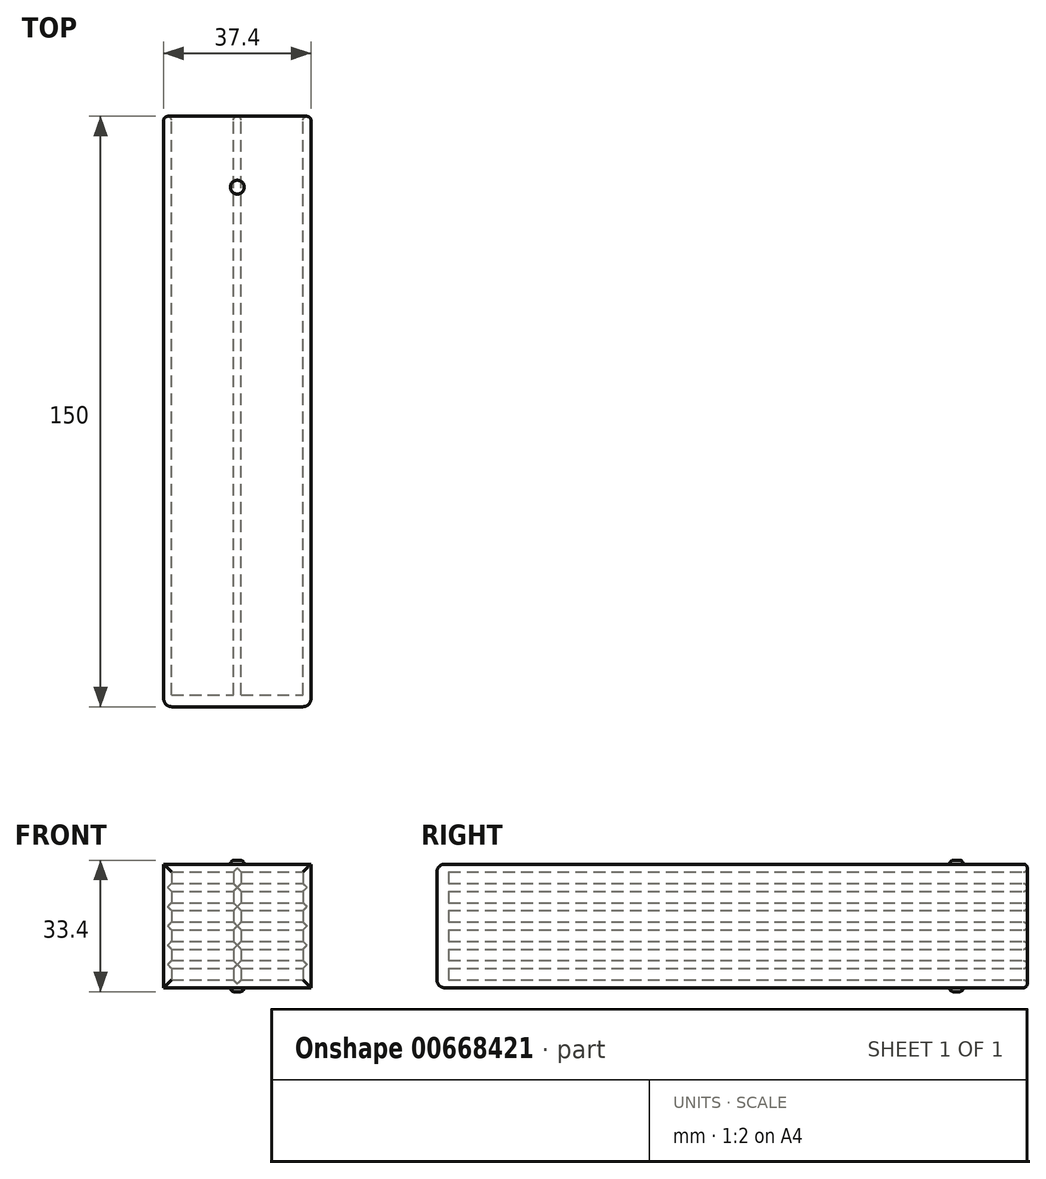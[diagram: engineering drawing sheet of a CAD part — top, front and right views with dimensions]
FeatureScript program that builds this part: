
annotation { "Feature Type Name" : "Feature", "Feature Type Description" : "" }
export const myFeature = defineFeature(function(context is Context, id is Id, definition is map)
    precondition{}
    {
        {
            var Q0;
            Q0=qCreatedBy(makeId("Front.planeOp"),FACE);
            var sketch = newSketch(context, id + "F0", { "sketchPlane" : qUnion([Q0])});
            skLineSegment(sketch, "E0.bottom", {"start": v(-15.7, -3.54) * mm, "end": v(0, -3.54) * mm});
            skLineSegment(sketch, "E0.top", {"start": v(-15.7, -6.44) * mm, "end": v(0, -6.44) * mm});
            skLineSegment(sketch, "E0.left", {"start": v(-15.7, -3.54) * mm, "end": v(-15.7, -6.44) * mm});
            skLineSegment(sketch, "E0.right", {"start": v(0, -3.54) * mm, "end": v(0, -6.44) * mm});
            skLineSegment(sketch, "E1.0.1.0", {"start": v(2, -3.54) * mm, "end": v(17.7, -3.54) * mm});
            skLineSegment(sketch, "E1.0.1.1", {"start": v(2, -6.44) * mm, "end": v(17.7, -6.44) * mm});
            skLineSegment(sketch, "E1.0.1.2", {"start": v(2, -3.54) * mm, "end": v(2, -6.44) * mm});
            skLineSegment(sketch, "E1.0.1.3", {"start": v(17.7, -3.54) * mm, "end": v(17.7, -6.44) * mm});
            skLineSegment(sketch, "E1.1.0.0", {"start": v(-15.7, -8.44) * mm, "end": v(0, -8.44) * mm});
            skLineSegment(sketch, "E1.1.0.1", {"start": v(-15.7, -11.34) * mm, "end": v(0, -11.34) * mm});
            skLineSegment(sketch, "E1.1.0.2", {"start": v(-15.7, -8.44) * mm, "end": v(-15.7, -11.34) * mm});
            skLineSegment(sketch, "E1.1.0.3", {"start": v(0, -8.44) * mm, "end": v(0, -11.34) * mm});
            skLineSegment(sketch, "E1.1.1.0", {"start": v(2, -8.44) * mm, "end": v(17.7, -8.44) * mm});
            skLineSegment(sketch, "E1.1.1.1", {"start": v(2, -11.34) * mm, "end": v(17.7, -11.34) * mm});
            skLineSegment(sketch, "E1.1.1.2", {"start": v(2, -8.44) * mm, "end": v(2, -11.34) * mm});
            skLineSegment(sketch, "E1.1.1.3", {"start": v(17.7, -8.44) * mm, "end": v(17.7, -11.34) * mm});
            skLineSegment(sketch, "E1.2.0.0", {"start": v(-15.7, -13.34) * mm, "end": v(0, -13.34) * mm});
            skLineSegment(sketch, "E1.2.0.1", {"start": v(-15.7, -16.24) * mm, "end": v(0, -16.24) * mm});
            skLineSegment(sketch, "E1.2.0.2", {"start": v(-15.7, -13.34) * mm, "end": v(-15.7, -16.24) * mm});
            skLineSegment(sketch, "E1.2.0.3", {"start": v(0, -13.34) * mm, "end": v(0, -16.24) * mm});
            skLineSegment(sketch, "E1.2.1.0", {"start": v(2, -13.34) * mm, "end": v(17.7, -13.34) * mm});
            skLineSegment(sketch, "E1.2.1.1", {"start": v(2, -16.24) * mm, "end": v(17.7, -16.24) * mm});
            skLineSegment(sketch, "E1.2.1.2", {"start": v(2, -13.34) * mm, "end": v(2, -16.24) * mm});
            skLineSegment(sketch, "E1.2.1.3", {"start": v(17.7, -13.34) * mm, "end": v(17.7, -16.24) * mm});
            skLineSegment(sketch, "E1.3.0.0", {"start": v(-15.7, -18.24) * mm, "end": v(0, -18.24) * mm});
            skLineSegment(sketch, "E1.3.0.1", {"start": v(-15.7, -21.14) * mm, "end": v(0, -21.14) * mm});
            skLineSegment(sketch, "E1.3.0.2", {"start": v(-15.7, -18.24) * mm, "end": v(-15.7, -21.14) * mm});
            skLineSegment(sketch, "E1.3.0.3", {"start": v(0, -18.24) * mm, "end": v(0, -21.14) * mm});
            skLineSegment(sketch, "E1.3.1.0", {"start": v(2, -18.24) * mm, "end": v(17.7, -18.24) * mm});
            skLineSegment(sketch, "E1.3.1.1", {"start": v(2, -21.14) * mm, "end": v(17.7, -21.14) * mm});
            skLineSegment(sketch, "E1.3.1.2", {"start": v(2, -18.24) * mm, "end": v(2, -21.14) * mm});
            skLineSegment(sketch, "E1.3.1.3", {"start": v(17.7, -18.24) * mm, "end": v(17.7, -21.14) * mm});
            skLineSegment(sketch, "E1.4.0.0", {"start": v(-15.7, -23.14) * mm, "end": v(0, -23.14) * mm});
            skLineSegment(sketch, "E1.4.0.1", {"start": v(-15.7, -26.04) * mm, "end": v(0, -26.04) * mm});
            skLineSegment(sketch, "E1.4.0.2", {"start": v(-15.7, -23.14) * mm, "end": v(-15.7, -26.04) * mm});
            skLineSegment(sketch, "E1.4.0.3", {"start": v(0, -23.14) * mm, "end": v(0, -26.04) * mm});
            skLineSegment(sketch, "E1.4.1.0", {"start": v(2, -23.14) * mm, "end": v(17.7, -23.14) * mm});
            skLineSegment(sketch, "E1.4.1.1", {"start": v(2, -26.04) * mm, "end": v(17.7, -26.04) * mm});
            skLineSegment(sketch, "E1.4.1.2", {"start": v(2, -23.14) * mm, "end": v(2, -26.04) * mm});
            skLineSegment(sketch, "E1.4.1.3", {"start": v(17.7, -23.14) * mm, "end": v(17.7, -26.04) * mm});
            skLineSegment(sketch, "E1.5.0.0", {"start": v(-15.7, -28.04) * mm, "end": v(0, -28.04) * mm});
            skLineSegment(sketch, "E1.5.0.1", {"start": v(-15.7, -30.94) * mm, "end": v(0, -30.94) * mm});
            skLineSegment(sketch, "E1.5.0.2", {"start": v(-15.7, -28.04) * mm, "end": v(-15.7, -30.94) * mm});
            skLineSegment(sketch, "E1.5.0.3", {"start": v(0, -28.04) * mm, "end": v(0, -30.94) * mm});
            skLineSegment(sketch, "E1.5.1.0", {"start": v(2, -28.04) * mm, "end": v(17.7, -28.04) * mm});
            skLineSegment(sketch, "E1.5.1.1", {"start": v(2, -30.94) * mm, "end": v(17.7, -30.94) * mm});
            skLineSegment(sketch, "E1.5.1.2", {"start": v(2, -28.04) * mm, "end": v(2, -30.94) * mm});
            skLineSegment(sketch, "E1.5.1.3", {"start": v(17.7, -28.04) * mm, "end": v(17.7, -30.94) * mm});
            skLineSegment(sketch, "E1.direction1", {"start": v(-15.7, -3.54) * mm, "end": v(-15.7, -8.44) * mm, "construction": true});
            skLineSegment(sketch, "E1.direction2", {"start": v(-15.7, -3.54) * mm, "end": v(2, -3.54) * mm, "construction": true});
            skLineSegment(sketch, "E2.bottom", {"start": v(-17.7, -1.54) * mm, "end": v(19.7, -1.54) * mm});
            skLineSegment(sketch, "E2.top", {"start": v(-17.7, -32.94) * mm, "end": v(19.7, -32.94) * mm});
            skLineSegment(sketch, "E2.left", {"start": v(-17.7, -1.54) * mm, "end": v(-17.7, -32.94) * mm});
            skLineSegment(sketch, "E2.right", {"start": v(19.7, -1.54) * mm, "end": v(19.7, -32.94) * mm});
            skSolve(sketch);
        }
        {
            var Q0;
            Q0 = qSketchRegion(id + "F0", true);
            extrude(context, id + "F1", {"entities" : qUnion([Q0]), "depth" : 147 * mm, "offsetDistance" : 25 * mm});
        }
        {
            var Q0;
            Q0=makeQuery(id+"F1.opExtrude","CAP_FACE",FACE,{"disambiguationData":[OSD([sQuery(id+"F0.wireOp",EDGE,"E0.bottom"),sQuery(id+"F0.wireOp",EDGE,"E0.top"),sQuery(id+"F0.wireOp",EDGE,"E0.left"),sQuery(id+"F0.wireOp",EDGE,"E0.right"),sQuery(id+"F0.wireOp",EDGE,"E1.0.1.0"),sQuery(id+"F0.wireOp",EDGE,"E1.0.1.1"),sQuery(id+"F0.wireOp",EDGE,"E1.0.1.2"),sQuery(id+"F0.wireOp",EDGE,"E1.0.1.3"),sQuery(id+"F0.wireOp",EDGE,"E1.1.0.0"),sQuery(id+"F0.wireOp",EDGE,"E1.1.0.1"),sQuery(id+"F0.wireOp",EDGE,"E1.1.0.2"),sQuery(id+"F0.wireOp",EDGE,"E1.1.0.3"),sQuery(id+"F0.wireOp",EDGE,"E1.1.1.0"),sQuery(id+"F0.wireOp",EDGE,"E1.1.1.1"),sQuery(id+"F0.wireOp",EDGE,"E1.1.1.2"),sQuery(id+"F0.wireOp",EDGE,"E1.1.1.3"),sQuery(id+"F0.wireOp",EDGE,"E1.2.0.0"),sQuery(id+"F0.wireOp",EDGE,"E1.2.0.1"),sQuery(id+"F0.wireOp",EDGE,"E1.2.0.2"),sQuery(id+"F0.wireOp",EDGE,"E1.2.0.3"),sQuery(id+"F0.wireOp",EDGE,"E1.2.1.0"),sQuery(id+"F0.wireOp",EDGE,"E1.2.1.1"),sQuery(id+"F0.wireOp",EDGE,"E1.2.1.2"),sQuery(id+"F0.wireOp",EDGE,"E1.2.1.3"),sQuery(id+"F0.wireOp",EDGE,"E1.3.0.0"),sQuery(id+"F0.wireOp",EDGE,"E1.3.0.1"),sQuery(id+"F0.wireOp",EDGE,"E1.3.0.2"),sQuery(id+"F0.wireOp",EDGE,"E1.3.0.3"),sQuery(id+"F0.wireOp",EDGE,"E1.3.1.0"),sQuery(id+"F0.wireOp",EDGE,"E1.3.1.1"),sQuery(id+"F0.wireOp",EDGE,"E1.3.1.2"),sQuery(id+"F0.wireOp",EDGE,"E1.3.1.3"),sQuery(id+"F0.wireOp",EDGE,"E1.4.0.0"),sQuery(id+"F0.wireOp",EDGE,"E1.4.0.1"),sQuery(id+"F0.wireOp",EDGE,"E1.4.0.2"),sQuery(id+"F0.wireOp",EDGE,"E1.4.0.3"),sQuery(id+"F0.wireOp",EDGE,"E1.4.1.0"),sQuery(id+"F0.wireOp",EDGE,"E1.4.1.1"),sQuery(id+"F0.wireOp",EDGE,"E1.4.1.2"),sQuery(id+"F0.wireOp",EDGE,"E1.4.1.3"),sQuery(id+"F0.wireOp",EDGE,"E1.5.0.0"),sQuery(id+"F0.wireOp",EDGE,"E1.5.0.1"),sQuery(id+"F0.wireOp",EDGE,"E1.5.0.2"),sQuery(id+"F0.wireOp",EDGE,"E1.5.0.3"),sQuery(id+"F0.wireOp",EDGE,"E1.5.1.0"),sQuery(id+"F0.wireOp",EDGE,"E1.5.1.1"),sQuery(id+"F0.wireOp",EDGE,"E1.5.1.2"),sQuery(id+"F0.wireOp",EDGE,"E1.5.1.3"),sQuery(id+"F0.wireOp",EDGE,"E2.bottom"),sQuery(id+"F0.wireOp",EDGE,"E2.top"),sQuery(id+"F0.wireOp",EDGE,"E2.left"),sQuery(id+"F0.wireOp",EDGE,"E2.right")])],"isStart":false});
            var sketch = newSketch(context, id + "F2", { "sketchPlane" : qUnion([Q0])});
            skLineSegment(sketch, "E3.bottom", {"start": v(-17.7, -1.54) * mm, "end": v(19.7, -1.54) * mm});
            skLineSegment(sketch, "E3.top", {"start": v(-17.7, -32.94) * mm, "end": v(19.7, -32.94) * mm});
            skLineSegment(sketch, "E3.left", {"start": v(-17.7, -1.54) * mm, "end": v(-17.7, -32.94) * mm});
            skLineSegment(sketch, "E3.right", {"start": v(19.7, -1.54) * mm, "end": v(19.7, -32.94) * mm});
            skSolve(sketch);
        }
        {
            var Q0;
            Q0 = qSketchRegion(id + "F2", true);
            extrude(context, id + "F3", {"entities" : qUnion([Q0]), "operationType" : NewBodyOperationType.ADD, "depth" : 3 * mm, "offsetDistance" : 25 * mm});
        }
        {
            var Q0;
            Q0=makeQuery(id+"F3.opExtrude","CAP_FACE",FACE,{"disambiguationData":[OSD([sQuery(id+"F2.wireOp",EDGE,"E3.bottom"),sQuery(id+"F2.wireOp",EDGE,"E3.top"),sQuery(id+"F2.wireOp",EDGE,"E3.left"),sQuery(id+"F2.wireOp",EDGE,"E3.right")])],"isStart":false});
            fillet(context, id + "F4", {"entities" : qUnion([Q0]), "radius" : 2 * mm, "tangentPropagation" : true, "allowEdgeOverflow" : false});
        }
        {
            var Q0;
            Q0=makeQuery(id+"F1.opExtrude","CAP_FACE",FACE,{"disambiguationData":[OSD([sQuery(id+"F0.wireOp",EDGE,"E0.bottom"),sQuery(id+"F0.wireOp",EDGE,"E0.top"),sQuery(id+"F0.wireOp",EDGE,"E0.left"),sQuery(id+"F0.wireOp",EDGE,"E0.right"),sQuery(id+"F0.wireOp",EDGE,"E1.0.1.0"),sQuery(id+"F0.wireOp",EDGE,"E1.0.1.1"),sQuery(id+"F0.wireOp",EDGE,"E1.0.1.2"),sQuery(id+"F0.wireOp",EDGE,"E1.0.1.3"),sQuery(id+"F0.wireOp",EDGE,"E1.1.0.0"),sQuery(id+"F0.wireOp",EDGE,"E1.1.0.1"),sQuery(id+"F0.wireOp",EDGE,"E1.1.0.2"),sQuery(id+"F0.wireOp",EDGE,"E1.1.0.3"),sQuery(id+"F0.wireOp",EDGE,"E1.1.1.0"),sQuery(id+"F0.wireOp",EDGE,"E1.1.1.1"),sQuery(id+"F0.wireOp",EDGE,"E1.1.1.2"),sQuery(id+"F0.wireOp",EDGE,"E1.1.1.3"),sQuery(id+"F0.wireOp",EDGE,"E1.2.0.0"),sQuery(id+"F0.wireOp",EDGE,"E1.2.0.1"),sQuery(id+"F0.wireOp",EDGE,"E1.2.0.2"),sQuery(id+"F0.wireOp",EDGE,"E1.2.0.3"),sQuery(id+"F0.wireOp",EDGE,"E1.2.1.0"),sQuery(id+"F0.wireOp",EDGE,"E1.2.1.1"),sQuery(id+"F0.wireOp",EDGE,"E1.2.1.2"),sQuery(id+"F0.wireOp",EDGE,"E1.2.1.3"),sQuery(id+"F0.wireOp",EDGE,"E1.3.0.0"),sQuery(id+"F0.wireOp",EDGE,"E1.3.0.1"),sQuery(id+"F0.wireOp",EDGE,"E1.3.0.2"),sQuery(id+"F0.wireOp",EDGE,"E1.3.0.3"),sQuery(id+"F0.wireOp",EDGE,"E1.3.1.0"),sQuery(id+"F0.wireOp",EDGE,"E1.3.1.1"),sQuery(id+"F0.wireOp",EDGE,"E1.3.1.2"),sQuery(id+"F0.wireOp",EDGE,"E1.3.1.3"),sQuery(id+"F0.wireOp",EDGE,"E1.4.0.0"),sQuery(id+"F0.wireOp",EDGE,"E1.4.0.1"),sQuery(id+"F0.wireOp",EDGE,"E1.4.0.2"),sQuery(id+"F0.wireOp",EDGE,"E1.4.0.3"),sQuery(id+"F0.wireOp",EDGE,"E1.4.1.0"),sQuery(id+"F0.wireOp",EDGE,"E1.4.1.1"),sQuery(id+"F0.wireOp",EDGE,"E1.4.1.2"),sQuery(id+"F0.wireOp",EDGE,"E1.4.1.3"),sQuery(id+"F0.wireOp",EDGE,"E1.5.0.0"),sQuery(id+"F0.wireOp",EDGE,"E1.5.0.1"),sQuery(id+"F0.wireOp",EDGE,"E1.5.0.2"),sQuery(id+"F0.wireOp",EDGE,"E1.5.0.3"),sQuery(id+"F0.wireOp",EDGE,"E1.5.1.0"),sQuery(id+"F0.wireOp",EDGE,"E1.5.1.1"),sQuery(id+"F0.wireOp",EDGE,"E1.5.1.2"),sQuery(id+"F0.wireOp",EDGE,"E1.5.1.3"),sQuery(id+"F0.wireOp",EDGE,"E2.bottom"),sQuery(id+"F0.wireOp",EDGE,"E2.top"),sQuery(id+"F0.wireOp",EDGE,"E2.left"),sQuery(id+"F0.wireOp",EDGE,"E2.right")])],"isStart":true});
            fillet(context, id + "F5", {"entities" : qUnion([Q0]), "radius" : 1 * mm, "tangentPropagation" : true, "allowEdgeOverflow" : false});
        }
        {
            var Q0;
            Q0=makeQuery(id+"F3.boolean.opBoolean","MERGE",FACE,{"derivedFrom":[makeQuery(id+"F1.opExtrude","SWEPT_FACE",FACE,{"disambiguationData":[OSD([sQuery(id+"F0.wireOp",EDGE,"E2.top")])]}),makeQuery(id+"F3.opExtrude","SWEPT_FACE",FACE,{"disambiguationData":[OSD([sQuery(id+"F2.wireOp",EDGE,"E3.top")])]})]});
            var sketch = newSketch(context, id + "F6", { "sketchPlane" : qUnion([Q0])});
            skText(sketch, "E4", { "text": "flat file", "fontName": "OpenSans-Bold.ttf"});
            const initialGuessF6  = {"E4": [-0.008, 0.14531, 0, -1, 0.015]};
            skSetInitialGuess(sketch, initialGuessF6);
            skSolve(sketch);
        }
        {
            var Q0;
            Q0=makeQuery(id+"F3.boolean.opBoolean","MERGE",FACE,{"derivedFrom":[makeQuery(id+"F1.opExtrude","SWEPT_FACE",FACE,{"disambiguationData":[OSD([sQuery(id+"F0.wireOp",EDGE,"E2.bottom")])]}),makeQuery(id+"F3.opExtrude","SWEPT_FACE",FACE,{"disambiguationData":[OSD([sQuery(id+"F2.wireOp",EDGE,"E3.bottom")])]})]});
            var sketch = newSketch(context, id + "F7", { "sketchPlane" : qUnion([Q0])});
            skLineSegment(sketch, "E5", {"start": v(-16.7, 0) * mm, "end": v(18.7, 0) * mm});
            skLineSegment(sketch, "E6", {"start": v(-30.07, -18) * mm, "end": v(37.03, -18) * mm, "construction": true});
            skCircle(sketch, "E7", {"center": v(1, -18) * mm, "radius": 1.75 * mm});
            skLineSegment(sketch, "E8", {"start": v(1, -1) * mm, "end": v(1, -24.07) * mm, "construction": true});
            skSolve(sketch);
        }
        {
            var Q0;
            Q0 = qSketchRegion(id + "F7", true);
            extrude(context, id + "F8", {"entities" : qUnion([Q0]), "operationType" : NewBodyOperationType.ADD, "depth" : 1 * mm, "offsetDistance" : 25 * mm});
        }
        {
            var Q0;
            Q0=makeQuery(id+"F8.opExtrude","CAP_EDGE",EDGE,{"disambiguationData":[OSD([sQuery(id+"F7.wireOp",EDGE,"E7")])],"isStart":false});
            fillet(context, id + "F9", {"entities" : qUnion([Q0]), "radius" : 1 * mm, "tangentPropagation" : true, "allowEdgeOverflow" : false});
        }
        {
            var Q0;
            Q0=makeQuery(id+"F3.boolean.opBoolean","MERGE",FACE,{"derivedFrom":[makeQuery(id+"F1.opExtrude","SWEPT_FACE",FACE,{"disambiguationData":[OSD([sQuery(id+"F0.wireOp",EDGE,"E2.bottom")])]}),makeQuery(id+"F3.opExtrude","SWEPT_FACE",FACE,{"disambiguationData":[OSD([sQuery(id+"F2.wireOp",EDGE,"E3.bottom")])]})]});
            var sketch = newSketch(context, id + "F10", { "sketchPlane" : qUnion([Q0])});
            skCircle(sketch, "E9.0", {"center": v(1, -18) * mm, "radius": 1.75 * mm});
            skCircle(sketch, "E9.1", {"center": v(1, -18) * mm, "radius": 0.75 * mm});
            skSolve(sketch);
        }
        {
            var Q0;
            Q0=makeQuery(id+"F6.imprint","IMPRINT",FACE,{"disambiguationData":[TD([[makeQuery(id+"F6.imprint","IMPRINT",EDGE,{"derivedFrom":sQuery(id+"F6.wireOp",EDGE,"E4.sketch_text.stroke-0")}),1.0]])]});
            var sketch = newSketch(context, id + "F11", { "sketchPlane" : qUnion([Q0])});
            skCircle(sketch, "E10.0", {"center": v(1, 18) * mm, "radius": 1.75 * mm});
            skSolve(sketch);
        }
        {
            var Q0;
            Q0 = qSketchRegion(id + "F11", true);
            extrude(context, id + "F12", {"entities" : qUnion([Q0]), "operationType" : NewBodyOperationType.ADD, "depth" : 1 * mm, "offsetDistance" : 25 * mm});
        }
        {
            var Q0;
            Q0=makeQuery(id+"F12.opExtrude","CAP_FACE",FACE,{"disambiguationData":[OSD([sQuery(id+"F11.wireOp",EDGE,"E10.0")])],"isStart":false});
            fillet(context, id + "F13", {"entities" : qUnion([Q0]), "radius" : 1 * mm, "tangentPropagation" : true, "allowEdgeOverflow" : false});
        }
    });
